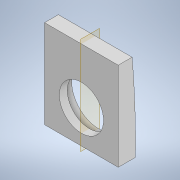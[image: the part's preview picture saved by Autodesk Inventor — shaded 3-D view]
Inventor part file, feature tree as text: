
AUTODESK INVENTOR PART (.ipt)
format: ipt  version: 2021.1 (Build 251245000, 245)  size: 676,864 bytes
history: native  units: in
note: dims shown in document units (in); Inventor stores cm internally (conversion verified against a paired STEP export)
features: sketch x5, extrude x4, plane x2, emboss x1, split x1
ambient origin geometry x8: Origin, YZ Plane, XZ Plane, XY Plane, X Axis, Y Axis, Z Axis, Center Point
bodies: Solid1 (feature_tree)
feature tree (13):
  extrude  "Extrusion1"  Depth=4.0in
  extrude  "Extrusion2"  Depth=22.0in
  plane  "Work Plane2"
  emboss  "Emboss1"
  plane  "Work Plane3"
  extrude  "Extrusion4"  Depth=22.0in
  extrude  "Extrusion5"  TaperAngle=0.0deg  [1 undecoded]
  split  "Split1"
  sketch  "Sketch1"  dims[d0=0.5in d1=4.0in]
  sketch  "Sketch2"  dims[d5=22.0in d6=4.0in]
  sketch  "Sketch4"  dims[d7=22.0in d8=2.4in]
  sketch  "Sketch5"  dims[d9=2.0in d10=0.0in]
  sketch  "Sketch6"  dims[d11=1.2in d12=1.5in d13=0.0in d14=0.0in d18=0.175in d19=0.05in d20=0.0in d21=0.125in d22=0.25in d23=0.0in d24=0.5875in d25=0.125in d26=0.0in d27=0.0in]
note: 1 required parameter value undecoded (feature->parameter linkage not recoverable at this tier; creation-order binding heuristic only, values carry confidence <= 0.55)
